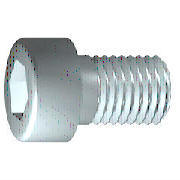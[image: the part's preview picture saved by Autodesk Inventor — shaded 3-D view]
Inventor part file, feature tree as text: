
AUTODESK INVENTOR PART (.ipt)
format: ipt  version: 2019 (Build 230136000, 136)  size: 204,288 bytes
history: native  units: mm (DEFAULTED — no unit token found)
features: sketch x2, extrude x1, plane x1, fillet x1
ambient origin geometry x7: Origin, YZ Plane, XY Plane, X Axis, Y Axis, Z Axis, Center Point
bodies: Solid1 (feature_tree), Body (feature_tree)
feature tree (5):
  extrude  "Slot"  Depth=3.0mm
  plane  "Work Plane1"
  fillet  "Fillet2"  Radius=3.0mm
  sketch  "Sketch1"  dims[d1=10.75mm d2=0.306825mm d3=3.0mm]
  sketch  "Sketch2"  dims[d4=1.3mm d5=60.0deg d6=3.0mm d7=3.0mm d8=2.886751mm d9=5.5mm d10=90.0deg d11=10.0mm d12=0.0mm d13=10.75mm d14=0.0mm d15=0.306725mm d16=0.306725mm d17=0.3mm d19=0.0mm d26=15.0mm d27=45.0deg d28=0.0mm d29=0.0mm d30=0.1mm]
